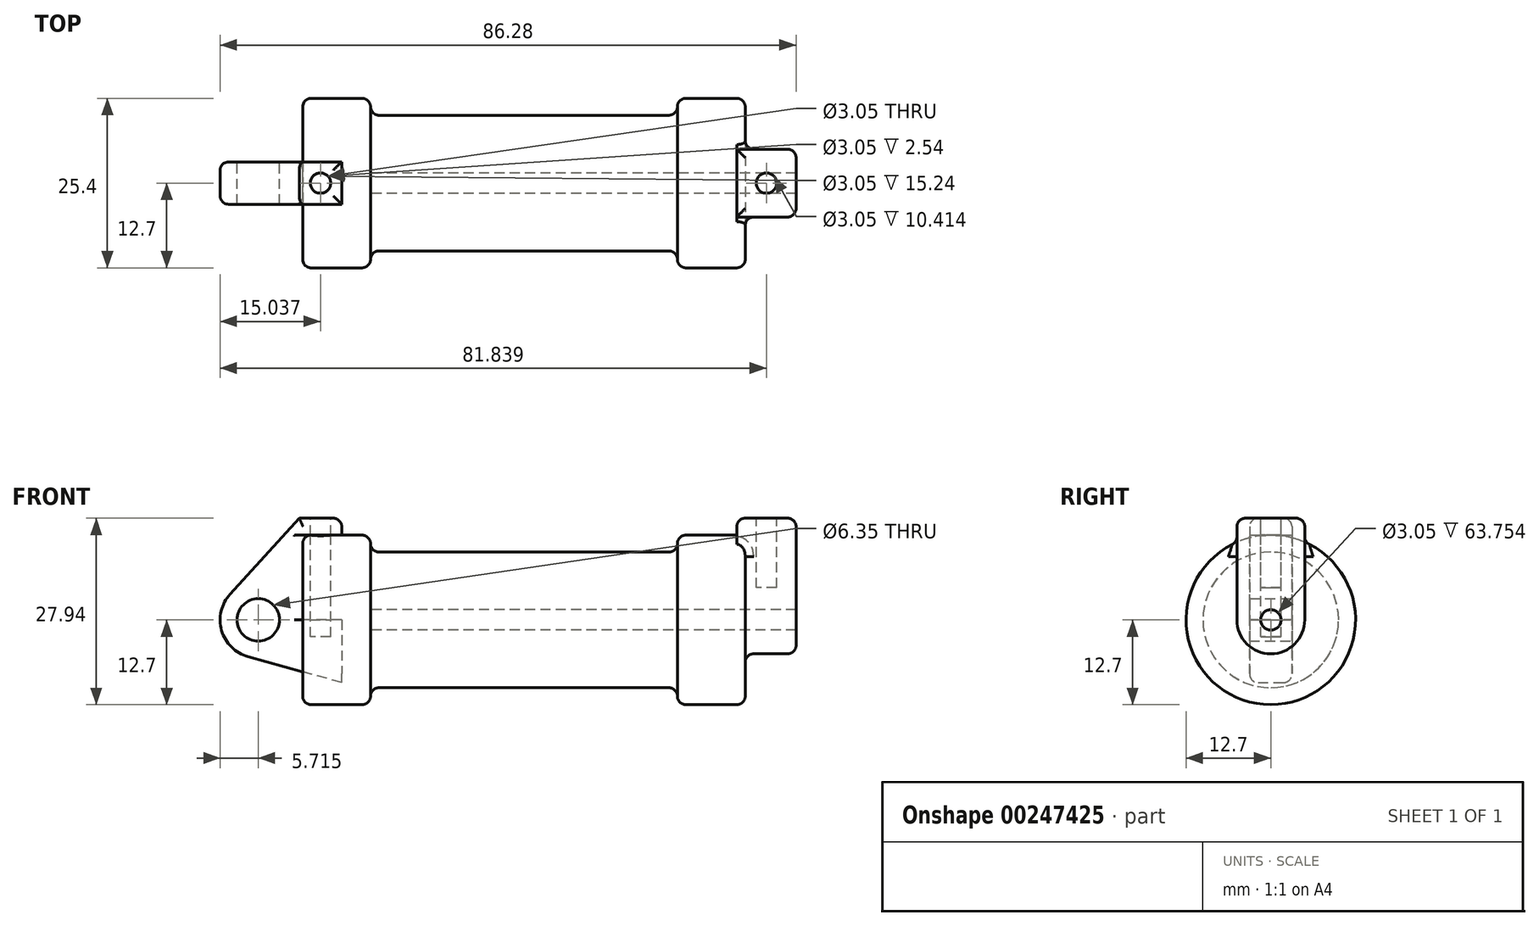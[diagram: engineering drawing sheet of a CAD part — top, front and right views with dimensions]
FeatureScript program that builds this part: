
annotation { "Feature Type Name" : "Feature", "Feature Type Description" : "" }
export const myFeature = defineFeature(function(context is Context, id is Id, definition is map)
    precondition{}
    {
        {
            var Q0;
            Q0=qCreatedBy(makeId("Front.planeOp"),FACE);
            var sketch = newSketch(context, id + "F0", { "sketchPlane" : qUnion([Q0])});
            skLineSegment(sketch, "E0", {"start": v(0, 0) * mm, "end": v(0, 12.7) * mm});
            skLineSegment(sketch, "E1", {"start": v(0, 12.7) * mm, "end": v(10.16, 12.7) * mm});
            skLineSegment(sketch, "E2", {"start": v(10.16, 12.7) * mm, "end": v(10.16, 10.16) * mm});
            skLineSegment(sketch, "E3", {"start": v(10.16, 10.16) * mm, "end": v(56.13, 10.16) * mm});
            skLineSegment(sketch, "E4", {"start": v(56.13, 10.16) * mm, "end": v(56.13, 12.7) * mm});
            skLineSegment(sketch, "E5", {"start": v(56.13, 12.7) * mm, "end": v(66.3, 12.7) * mm});
            skLineSegment(sketch, "E6", {"start": v(66.3, 12.7) * mm, "end": v(66.3, 0) * mm});
            skLineSegment(sketch, "E7", {"start": v(66.3, 0) * mm, "end": v(0, 0) * mm});
            skLineSegment(sketch, "E8", {"start": v(5.84, 15.24) * mm, "end": v(-0.5, 15.24) * mm});
            skLineSegment(sketch, "E9", {"start": v(-0.5, 15.24) * mm, "end": v(-10.88, 3.85) * mm});
            skLineSegment(sketch, "E10", {"start": v(0, 0) * mm, "end": v(-6.65, 0) * mm});
            skCircle(sketch, "E11", {"center": v(-6.65, 0) * mm, "radius": 5.72 * mm});
            skCircle(sketch, "E12", {"center": v(-6.65, 0) * mm, "radius": 3.18 * mm});
            skLineSegment(sketch, "E13", {"start": v(5.84, 15.24) * mm, "end": v(5.84, -9.4) * mm});
            skLineSegment(sketch, "E14", {"start": v(5.84, -9.4) * mm, "end": v(-8.18, -5.5) * mm});
            skSolve(sketch);
        }
        {
            var Q0;
            {var subQ0=sQuery(id+"F0.wireOp",EDGE,"E2");Q0=makeQuery(id+"F0.imprint","IMPRINT",FACE,{"disambiguationData":[TD([[makeQuery(id+"F0.imprint","IMPRINT",EDGE,{"derivedFrom":subQ0}),-1.0]])]});}
            var Q1;
            {var subQ0=sQuery(id+"F0.wireOp",EDGE,"E0");Q1=makeQuery(id+"F0.imprint","IMPRINT",FACE,{"disambiguationData":[TD([[makeQuery(id+"F0.imprint","IMPRINT",EDGE,{"derivedFrom":subQ0}),-1.0]])]});}
            var Q2;
            Q2=sQuery(id+"F0.wireOp",EDGE,"E7");
            revolve(context, id + "F1", {"entities" : qUnion([Q0, Q1]), "axis" : qUnion([Q2]), "revolveType" : RevolveType.FULL});
        }
        {
            var Q0;
            {var subQ4=sQuery(id+"F0.wireOp",EDGE,"E12");Q0=makeQuery(id+"F0.imprint","IMPRINT",FACE,{"disambiguationData":[TD([[makeQuery(id+"F0.imprint","IMPRINT",EDGE,{"derivedFrom":subQ4}),-1.0]])]});}
            var Q1;
            {var subQ0=sQuery(id+"F0.wireOp",EDGE,"E14");Q1=makeQuery(id+"F0.imprint","IMPRINT",FACE,{"disambiguationData":[TD([[makeQuery(id+"F0.imprint","IMPRINT",EDGE,{"derivedFrom":subQ0}),-1.0]])]});}
            var Q2;
            {var subQ3=sQuery(id+"F0.wireOp",EDGE,"E0");Q2=makeQuery(id+"F0.imprint","IMPRINT",FACE,{"disambiguationData":[TD([[makeQuery(id+"F0.imprint","IMPRINT",EDGE,{"derivedFrom":subQ3}),1.0]])]});}
            extrude(context, id + "F2", {"entities" : qUnion([Q0, Q1, Q2]), "endBound" : BoundingType.SYMMETRIC, "depth" : 6.35 * mm});
        }
        {
            var Q0;
            Q0=makeQuery(id+"F1.opRevolve","SWEPT_FACE",FACE,{"disambiguationData":[OSD([sQuery(id+"F0.wireOp",EDGE,"E6")])]});
            var sketch = newSketch(context, id + "F3", { "sketchPlane" : qUnion([Q0])});
            skCircle(sketch, "E15", {"center": v(0, 0) * mm, "radius": 1.52 * mm});
            skCircle(sketch, "E16", {"center": v(0, 0) * mm, "radius": 5.08 * mm});
            skLineSegment(sketch, "E17", {"start": v(5.08, 0) * mm, "end": v(5.08, 15.24) * mm});
            skLineSegment(sketch, "E18", {"start": v(5.08, 15.24) * mm, "end": v(-5.08, 15.24) * mm});
            skLineSegment(sketch, "E19", {"start": v(-5.08, 15.24) * mm, "end": v(-5.08, 0) * mm});
            skSolve(sketch);
        }
        {
            var Q0;
            Q0=makeQuery(id+"F3.imprint","IMPRINT",FACE,{"disambiguationData":[TD([[makeQuery(id+"F3.imprint","IMPRINT",EDGE,{"derivedFrom":sQuery(id+"F3.wireOp",EDGE,"E15")}),-1.0]])]});
            var Q1;
            {var subQ0=sQuery(id+"F3.wireOp",EDGE,"E17");var subQ1=sQuery(id+"F3.wireOp",EDGE,"E16");var subQ2=makeQuery(id+"F3.imprint","INTERSECT",VERTEX,{"derivedFrom":[subQ1,subQ0]});Q1=makeQuery(id+"F3.imprint","IMPRINT",FACE,{"disambiguationData":[TD([[makeQuery(id+"F3.imprint","IMPRINT",EDGE,{"disambiguationData":[TD([[subQ2,-1.0]])],"derivedFrom":subQ1}),-1.0]])]});}
            var Q2;
            {var subQ0=sQuery(id+"F3.wireOp",EDGE,"E18");Q2=makeQuery(id+"F3.imprint","IMPRINT",FACE,{"disambiguationData":[TD([[makeQuery(id+"F3.imprint","IMPRINT",EDGE,{"derivedFrom":subQ0}),1.0]])]});}
            extrude(context, id + "F4", {"entities" : qUnion([Q0, Q1, Q2]), "operationType" : NewBodyOperationType.ADD, "depth" : 7.62 * mm});
        }
        {
            var Q0;
            Q0=makeQuery(id+"F4.opExtrude","CAP_FACE",FACE,{"disambiguationData":[OSD([sQuery(id+"F3.wireOp",EDGE,"E15"),sQuery(id+"F3.wireOp",EDGE,"E16"),sQuery(id+"F3.wireOp",EDGE,"E17"),sQuery(id+"F3.wireOp",EDGE,"E18"),sQuery(id+"F3.wireOp",EDGE,"E19")])],"isStart":true});
            extrude(context, id + "F5", {"entities" : qUnion([Q0]), "operationType" : NewBodyOperationType.ADD, "depth" : 1.27 * mm});
        }
        {
            var Q0;
            Q0=makeQuery(id+"F4.boolean.opBoolean","SPLIT",FACE,{"disambiguationData":[TD([makeQuery(id+"F4.opExtrude","SWEPT_FACE",FACE,{"disambiguationData":[OSD([sQuery(id+"F3.wireOp",EDGE,"E15")])]})])],"derivedFrom":makeQuery(id+"F1.opRevolve","SWEPT_FACE",FACE,{"disambiguationData":[OSD([sQuery(id+"F0.wireOp",EDGE,"E6")])]})});
            var Q1;
            Q1=makeQuery(id+"F1.opRevolve","SWEPT_FACE",FACE,{"disambiguationData":[OSD([sQuery(id+"F0.wireOp",EDGE,"E2")])]});
            extrude(context, id + "F6", {"entities" : qUnion([Q0]), "operationType" : NewBodyOperationType.REMOVE, "endBound" : BoundingType.UP_TO_SURFACE, "oppositeDirection" : true, "endBoundEntityFace" : qUnion([Q1]), "depth" : 25.4 * mm});
        }
        {
            var Q0;
            Q0=makeQuery(id+"F2.opExtrude","SWEPT_FACE",FACE,{"disambiguationData":[OSD([sQuery(id+"F0.wireOp",EDGE,"E8")])]});
            var sketch = newSketch(context, id + "F7", { "sketchPlane" : qUnion([Q0])});
            skCircle(sketch, "E20", {"center": v(2.67, 0) * mm, "radius": 1.52 * mm});
            skLineSegment(sketch, "E21", {"start": v(-0.5, 3.18) * mm, "end": v(5.84, -3.18) * mm, "construction": true});
            skSolve(sketch);
        }
        {
            var Q0;
            {var subQ0=sQuery(id+"F3.wireOp",EDGE,"E18");Q0=makeQuery(id+"F5.boolean.opBoolean","MERGE",FACE,{"derivedFrom":[makeQuery(id+"F4.opExtrude","SWEPT_FACE",FACE,{"disambiguationData":[OSD([subQ0])]}),makeQuery(id+"F5.opExtrude","SWEPT_FACE",FACE,{"disambiguationData":[OSD([subQ0])]})]});}
            var sketch = newSketch(context, id + "F8", { "sketchPlane" : qUnion([Q0])});
            skCircle(sketch, "E22", {"center": v(69.47, 0) * mm, "radius": 1.52 * mm});
            skLineSegment(sketch, "E23", {"start": v(65.02, 5.08) * mm, "end": v(73.91, -5.08) * mm, "construction": true});
            skSolve(sketch);
        }
        {
            var Q0;
            Q0=makeQuery(id+"F7.imprint","IMPRINT",FACE,{"disambiguationData":[TD([[makeQuery(id+"F7.imprint","IMPRINT",EDGE,{"derivedFrom":sQuery(id+"F7.wireOp",EDGE,"E20")}),1.0]])]});
            extrude(context, id + "F9", {"entities" : qUnion([Q0]), "operationType" : NewBodyOperationType.REMOVE, "oppositeDirection" : true, "depth" : 17.78 * mm});
        }
        {
            var Q0;
            Q0=makeQuery(id+"F8.imprint","IMPRINT",FACE,{"disambiguationData":[TD([[makeQuery(id+"F8.imprint","IMPRINT",EDGE,{"derivedFrom":sQuery(id+"F8.wireOp",EDGE,"E22")}),1.0]])]});
            var Q1;
            Q1=sQuery(id+"F8.wireOp",EDGE,"E22");
            extrude(context, id + "F10", {"entities" : qUnion([Q0]), "operationType" : NewBodyOperationType.REMOVE, "surfaceEntities" : qUnion([Q1]), "oppositeDirection" : true, "depth" : 10.4 * mm});
        }
        {
            var Q0;
            Q0=makeQuery(id+"F1.opRevolve","SWEPT_EDGE",EDGE,{"disambiguationData":[OSD([sQuery(id+"F0.wireOp",EDGE,"E2"),sQuery(id+"F0.wireOp",EDGE,"E3")])]});
            var Q1;
            Q1=makeQuery(id+"F1.opRevolve","SWEPT_EDGE",EDGE,{"disambiguationData":[OSD([sQuery(id+"F0.wireOp",EDGE,"E1"),sQuery(id+"F0.wireOp",EDGE,"E2")])]});
            var Q2;
            Q2=makeQuery(id+"F1.opRevolve","SWEPT_EDGE",EDGE,{"disambiguationData":[OSD([sQuery(id+"F0.wireOp",EDGE,"E0"),sQuery(id+"F0.wireOp",EDGE,"E1")])]});
            var Q3;
            Q3=makeQuery(id+"F1.opRevolve","SWEPT_EDGE",EDGE,{"disambiguationData":[OSD([sQuery(id+"F0.wireOp",EDGE,"E4"),sQuery(id+"F0.wireOp",EDGE,"E5")])]});
            var Q4;
            Q4=makeQuery(id+"F1.opRevolve","SWEPT_EDGE",EDGE,{"disambiguationData":[OSD([sQuery(id+"F0.wireOp",EDGE,"E3"),sQuery(id+"F0.wireOp",EDGE,"E4")])]});
            var Q5;
            Q5=makeQuery(id+"F4.boolean.opBoolean","SPLIT",EDGE,{"disambiguationData":[OD(1.0)],"derivedFrom":makeQuery(id+"F1.opRevolve","SWEPT_EDGE",EDGE,{"disambiguationData":[OSD([sQuery(id+"F0.wireOp",EDGE,"E5"),sQuery(id+"F0.wireOp",EDGE,"E6")])]})});
            var Q6;
            Q6=makeQuery(id+"F2.opExtrude","CAP_EDGE",EDGE,{"disambiguationData":[OSD([sQuery(id+"F0.wireOp",EDGE,"E11")])],"isStart":false});
            var Q7;
            Q7=makeQuery(id+"F2.opExtrude","CAP_EDGE",EDGE,{"disambiguationData":[OSD([sQuery(id+"F0.wireOp",EDGE,"E11")])],"isStart":true});
            var Q8;
            Q8=makeQuery(id+"F2.opExtrude","CAP_EDGE",EDGE,{"disambiguationData":[OSD([sQuery(id+"F0.wireOp",EDGE,"E0")])],"isStart":true});
            var Q9;
            Q9=makeQuery(id+"F2.opExtrude","CAP_EDGE",EDGE,{"disambiguationData":[OSD([sQuery(id+"F0.wireOp",EDGE,"E0")])],"isStart":false});
            var Q10;
            Q10=makeQuery(id+"F2.opExtrude","CAP_EDGE",EDGE,{"disambiguationData":[OSD([sQuery(id+"F0.wireOp",EDGE,"E8")])],"isStart":false});
            var Q11;
            Q11=makeQuery(id+"F2.opExtrude","SWEPT_EDGE",EDGE,{"disambiguationData":[OSD([sQuery(id+"F0.wireOp",EDGE,"E8"),sQuery(id+"F0.wireOp",EDGE,"E13")])]});
            var Q12;
            Q12=makeQuery(id+"F2.opExtrude","CAP_EDGE",EDGE,{"disambiguationData":[OSD([sQuery(id+"F0.wireOp",EDGE,"E8")])],"isStart":true});
            var Q13;
            Q13=makeQuery(id+"F4.opExtrude","CAP_EDGE",EDGE,{"disambiguationData":[OSD([sQuery(id+"F3.wireOp",EDGE,"E19")])],"isStart":false});
            var Q14;
            {var subQ0=sQuery(id+"F3.wireOp",EDGE,"E16");var subQ1=sQuery(id+"F3.wireOp",EDGE,"E19");Q14=makeQuery(id+"F4.boolean.opBoolean","SPLIT",EDGE,{"disambiguationData":[TD([makeQuery(id+"F4.opExtrude","SWEPT_FACE",FACE,{"disambiguationData":[OSD([subQ0])]})])],"derivedFrom":makeQuery(id+"F4.opExtrude","CAP_EDGE",EDGE,{"disambiguationData":[OSD([subQ1])],"isStart":true})});}
            var Q15;
            {var subQ0=sQuery(id+"F3.wireOp",EDGE,"E18");var subQ1=sQuery(id+"F3.wireOp",EDGE,"E17");Q15=makeQuery(id+"F5.boolean.opBoolean","MERGE",EDGE,{"derivedFrom":[makeQuery(id+"F4.opExtrude","SWEPT_EDGE",EDGE,{"disambiguationData":[OSD([subQ1,subQ0])]}),makeQuery(id+"F5.opExtrude","SWEPT_EDGE",EDGE,{"disambiguationData":[OSD([subQ1,subQ0])]})]});}
            var Q16;
            Q16=makeQuery(id+"F4.opExtrude","CAP_EDGE",EDGE,{"disambiguationData":[OSD([sQuery(id+"F3.wireOp",EDGE,"E18")])],"isStart":false});
            var Q17;
            {var subQ0=sQuery(id+"F3.wireOp",EDGE,"E19");var subQ1=sQuery(id+"F3.wireOp",EDGE,"E18");Q17=makeQuery(id+"F5.boolean.opBoolean","MERGE",EDGE,{"derivedFrom":[makeQuery(id+"F4.opExtrude","SWEPT_EDGE",EDGE,{"disambiguationData":[OSD([subQ1,subQ0])]}),makeQuery(id+"F5.opExtrude","SWEPT_EDGE",EDGE,{"disambiguationData":[OSD([subQ1,subQ0])]})]});}
            var Q18;
            Q18=makeQuery(id+"F5.opExtrude","CAP_EDGE",EDGE,{"disambiguationData":[OSD([sQuery(id+"F3.wireOp",EDGE,"E18")])],"isStart":false});
            fillet(context, id + "F11", {"entities" : qUnion([Q0, Q1, Q2, Q3, Q4, Q5, Q6, Q7, Q8, Q9, Q10, Q11, Q12, Q13, Q14, Q15, Q16, Q17, Q18]), "radius" : 1.27 * mm, "tangentPropagation" : true, "allowEdgeOverflow" : false});
        }
    });
